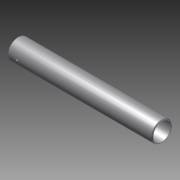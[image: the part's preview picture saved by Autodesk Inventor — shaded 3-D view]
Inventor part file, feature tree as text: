
AUTODESK INVENTOR PART (.ipt)
format: ipt  version: 2012 (Build 160160000, 160)  size: 134,144 bytes
history: native  units: in
note: dims shown in document units (in); Inventor stores cm internally (conversion verified against a paired STEP export)
features: other x42, sketch x2, revolve x1, extrude x1
ambient origin geometry x8: Origin, YZ Plane, XZ Plane, XY Plane, X Axis, Y Axis, Z Axis, Center Point
bodies: Solid1 (feature_tree)
feature tree (46):
  revolve  "Revolution1"  [1 undecoded]
  extrude  "Extrusion1"  [1 undecoded]
  other  "tube_front_XY"
  other  "tube_front_YZ"
  other  "tube_front_ZX"
  other  "tube_front_X"
  other  "tube_front_Y"
  other  "tube_front_Z"
  other  "tube_front_Center"
  other  "tube_rear_XY"
  other  "tube_rear_YZ"
  other  "tube_rear_ZX"
  other  "tube_rear_X"
  other  "tube_rear_Y"
  other  "tube_rear_Z"
  other  "tube_rear_Center"
  other  "cp1_XY"
  other  "cp1_YZ"
  other  "cp1_ZX"
  other  "cp1_X"
  other  "cp1_Y"
  other  "cp1_Z"
  other  "cp1_Center"
  other  "cp2_XY"
  other  "cp2_YZ"
  other  "cp2_ZX"
  other  "cp2_X"
  other  "cp2_Y"
  other  "cp2_Z"
  other  "cp2_Center"
  other  "cp3_XY"
  other  "cp3_YZ"
  other  "cp3_ZX"
  other  "cp3_X"
  other  "cp3_Y"
  other  "cp3_Z"
  other  "cp3_Center"
  other  "cp4_XY"
  other  "cp4_YZ"
  other  "cp4_ZX"
  other  "cp4_X"
  other  "cp4_Y"
  other  "cp4_Z"
  other  "cp4_Center"
  sketch  "Sketch_1"  dims[d0=360.0deg d1=0.4025in d2=0.0in]
  sketch  "Sketch_4"
note: 2 required parameter values undecoded (feature->parameter linkage not recoverable at this tier; creation-order binding heuristic only, values carry confidence <= 0.55)